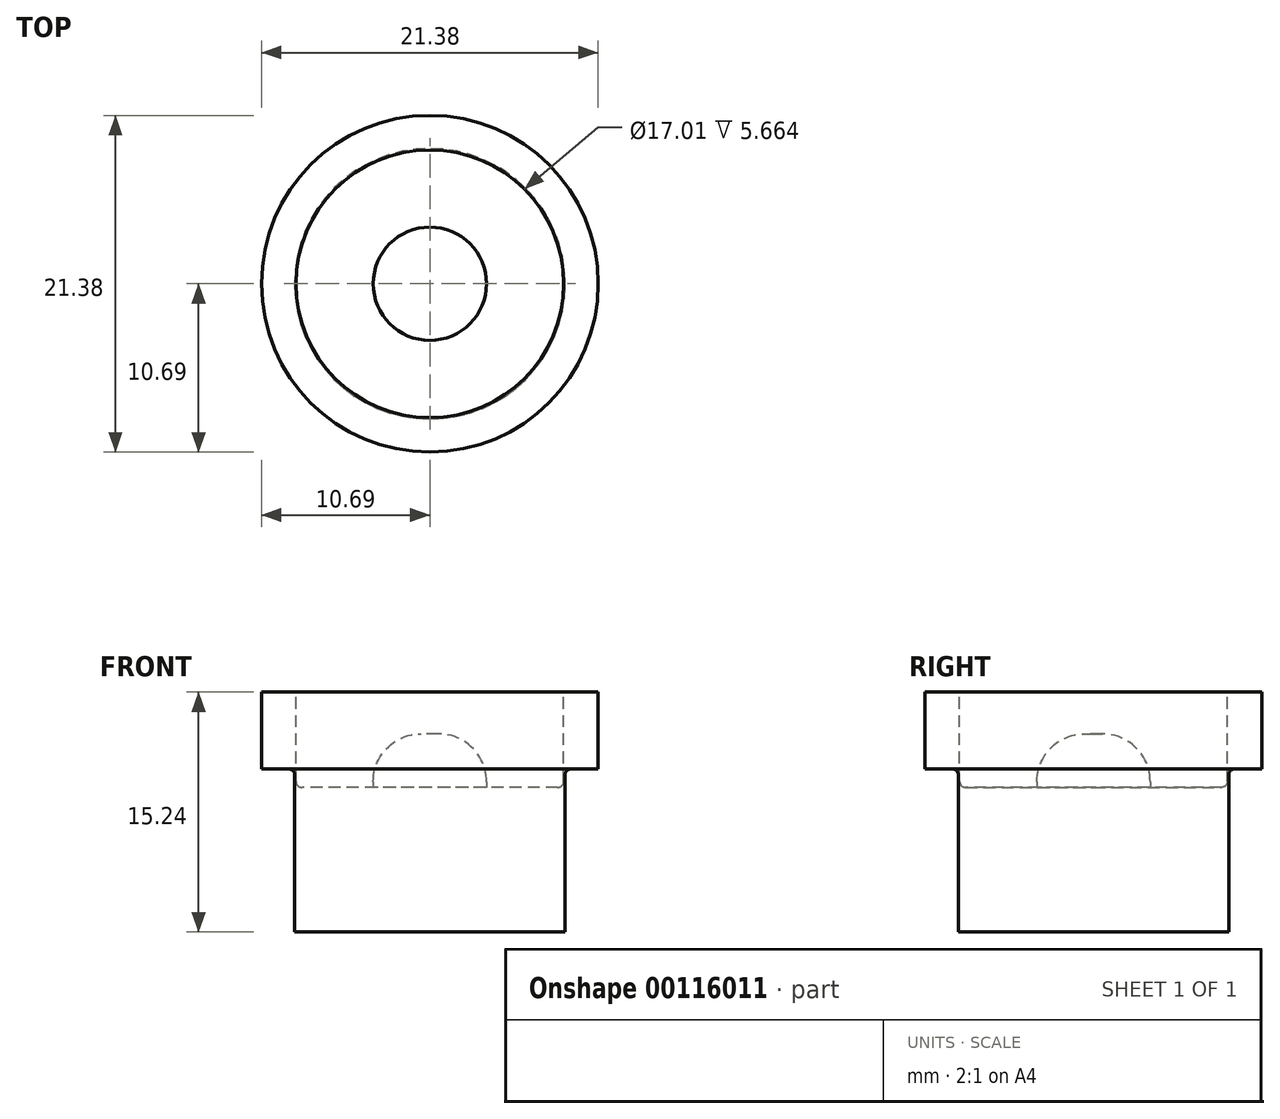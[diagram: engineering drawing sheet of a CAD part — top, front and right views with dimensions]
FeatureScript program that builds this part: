
annotation { "Feature Type Name" : "Feature", "Feature Type Description" : "" }
export const myFeature = defineFeature(function(context is Context, id is Id, definition is map)
    precondition{}
    {
        {
            var Q0;
            Q0=qCreatedBy(makeId("Front.planeOp"),FACE);
            var sketch = newSketch(context, id + "F0", { "sketchPlane" : qUnion([Q0])});
            skLineSegment(sketch, "E0", {"start": v(0, 7.9) * mm, "end": v(-10.7, 7.9) * mm});
            skLineSegment(sketch, "E1", {"start": v(-10.7, 7.9) * mm, "end": v(-10.7, 3.03) * mm});
            skLineSegment(sketch, "E2", {"start": v(-10.7, 3.03) * mm, "end": v(-8.59, 3.03) * mm});
            skLineSegment(sketch, "E3", {"start": v(-8.59, 3.03) * mm, "end": v(-8.59, -7.33) * mm});
            skLineSegment(sketch, "E4", {"start": v(-8.59, -7.33) * mm, "end": v(0, -7.33) * mm});
            skLineSegment(sketch, "E5", {"start": v(0, -7.33) * mm, "end": v(0, 7.9) * mm});
            skSolve(sketch);
        }
        {
            var Q0;
            Q0=makeQuery(id+"F0.imprint","IMPRINT",FACE,{"disambiguationData":[TD([[makeQuery(id+"F0.imprint","IMPRINT",EDGE,{"derivedFrom":sQuery(id+"F0.wireOp",EDGE,"E0")}),1.0]])]});
            var Q1;
            Q1=sQuery(id+"F0.wireOp",EDGE,"E4");
            var Q2;
            Q2=sQuery(id+"F0.wireOp",EDGE,"E0");
            var Q3;
            Q3=sQuery(id+"F0.wireOp",EDGE,"E3");
            var Q4;
            Q4=sQuery(id+"F0.wireOp",EDGE,"E5");
            var Q5;
            Q5=sQuery(id+"F0.wireOp",EDGE,"E1");
            var Q6;
            Q6=sQuery(id+"F0.wireOp",EDGE,"E2");
            var Q7;
            Q7=sQuery(id+"F0.wireOp",EDGE,"E5");
            revolve(context, id + "F1", {"entities" : qUnion([Q0]), "surfaceEntities" : qUnion([Q1, Q2, Q3, Q4, Q5, Q6]), "axis" : qUnion([Q7]), "revolveType" : RevolveType.FULL});
        }
        {
            var Q0;
            Q0=makeQuery(id+"F1.opRevolve","SWEPT_FACE",FACE,{"disambiguationData":[OSD([sQuery(id+"F0.wireOp",EDGE,"E0")])]});
            var sketch = newSketch(context, id + "F2", { "sketchPlane" : qUnion([Q0])});
            skCircle(sketch, "E6", {"center": v(0, 0) * mm, "radius": 8.5 * mm});
            skSolve(sketch);
        }
        {
            var Q0;
            Q0 = qSketchRegion(id + "F2", true);
            extrude(context, id + "F3", {"entities" : qUnion([Q0]), "operationType" : NewBodyOperationType.REMOVE, "oppositeDirection" : true, "depth" : 6.05 * mm});
        }
        {
            var Q0;
            Q0=makeQuery(id+"F3.boolean.opBoolean","COPY",FACE,{"derivedFrom":makeQuery(id+"F3.opExtrude","CAP_FACE",FACE,{"disambiguationData":[OSD([sQuery(id+"F2.wireOp",EDGE,"E6")])],"isStart":false})});
            var sketch = newSketch(context, id + "F4", { "sketchPlane" : qUnion([Q0])});
            skCircle(sketch, "E7", {"center": v(0, 0) * mm, "radius": 3.6 * mm});
            skSolve(sketch);
        }
        {
            var Q0;
            Q0 = qSketchRegion(id + "F4", true);
            extrude(context, id + "F5", {"entities" : qUnion([Q0]), "operationType" : NewBodyOperationType.ADD, "depth" : 3.4 * mm});
        }
        {
            var Q0;
            Q0=makeQuery(id+"F5.opExtrude","CAP_EDGE",EDGE,{"disambiguationData":[OSD([sQuery(id+"F4.wireOp",EDGE,"E7")])],"isStart":false});
            fillet(context, id + "F6", {"entities" : qUnion([Q0]), "radius" : 3.05 * mm, "tangentPropagation" : true, "allowEdgeOverflow" : false});
        }
        {
            var Q0;
            Q0=makeQuery(id+"F3.boolean.opBoolean","COPY",EDGE,{"derivedFrom":makeQuery(id+"F3.opExtrude","CAP_EDGE",EDGE,{"disambiguationData":[OSD([sQuery(id+"F2.wireOp",EDGE,"E6")])],"isStart":false})});
            var Q1;
            Q1=makeQuery(id+"F1.opRevolve","SWEPT_EDGE",EDGE,{"disambiguationData":[OSD([sQuery(id+"F0.wireOp",EDGE,"E2"),sQuery(id+"F0.wireOp",EDGE,"E3")])]});
            fillet(context, id + "F7", {"entities" : qUnion([Q0, Q1]), "radius" : 0.38 * mm, "tangentPropagation" : true, "allowEdgeOverflow" : false});
        }
    });
